# Revit family: Finestra ad una anta con persiana
name_source: partatom
category: Windows
revit_build: Autodesk Revit Architecture 2012 (Build: 20110309_2315(x64)
units: mm (PartAtom-declared; Revit-internal decimal feet)

## types (2) — shared parameters
Altezza Cassonetto = 300 mm  [stored 0.984252 ft]
Altezza da terra = 860 mm  [stored 2.82152 ft]
Apertura Persiane 3D DX = 90.00°
Apertura Persiane DX = 0.00°
Cassonetto = No
Dist.est.muro = 150 mm
Finestra-Listelli = Finestre - Telai  bianco
Finestra-Maniglia = Finestre - Maniglia
Finestra-Persiane = Finestre - Telai  bianco
Finestra-Soglia = Finestre - Soglia
Finestra-Telaio = Finestre - Telai  bianco
Finestra-Vetro = Finestre - Vetro
Finestre-Cassonetto = Finestre - Cassonetto
Imposta Finestra = 900 mm  [stored 2.95276 ft]
Listelli = No
N°Listelli Orizzontali = 4
N°Listelli Verticali = 2
Operation = Finestra 1 Anta
Persiane = Yes
Rientranza Cassonetto = 150 mm
Rough Width = 700 mm  [stored 2.29659 ft]
Sp.dav. = 40 mm  [stored 0.131234 ft]
Spessore Listelli Verticali = 15 mm  [stored 0.0492126 ft]
Sporg.DX.dav. = 40 mm  [stored 0.131234 ft]
Sporg.SX.dav. = 40 mm  [stored 0.131234 ft]
Sporg.est.dav. = 40 mm  [stored 0.131234 ft]
Sporg.int.dav. = 20 mm  [stored 0.0656168 ft]
Sporgenza Cassonetto = 200 mm  [stored 0.656168 ft]
Wall Closure = By host
Width = 600 mm  [stored 1.9685 ft]

## per-type parameters (varying)
| type | Altezza infisso | Height | Imposta Cassonetto | Rough Height |
| L60-H150 | 1500 mm  [stored 4.92126 ft] | 1500 mm  [stored 4.92126 ft] | 2400 mm  [stored 7.87402 ft] | 1460 mm |
| L60-H80 | 800 mm  [stored 2.62467 ft] | 800 mm  [stored 2.62467 ft] | 1700 mm  [stored 5.57743 ft] | 760 mm |

note: [stored X ft] marks values corroborated as IEEE doubles in the binary element streams (Revit-internal decimal feet)

## geometry (parser evidence)
native form markers: Blend x3, Sweep x4
no freeform markers — native parametric forms only
